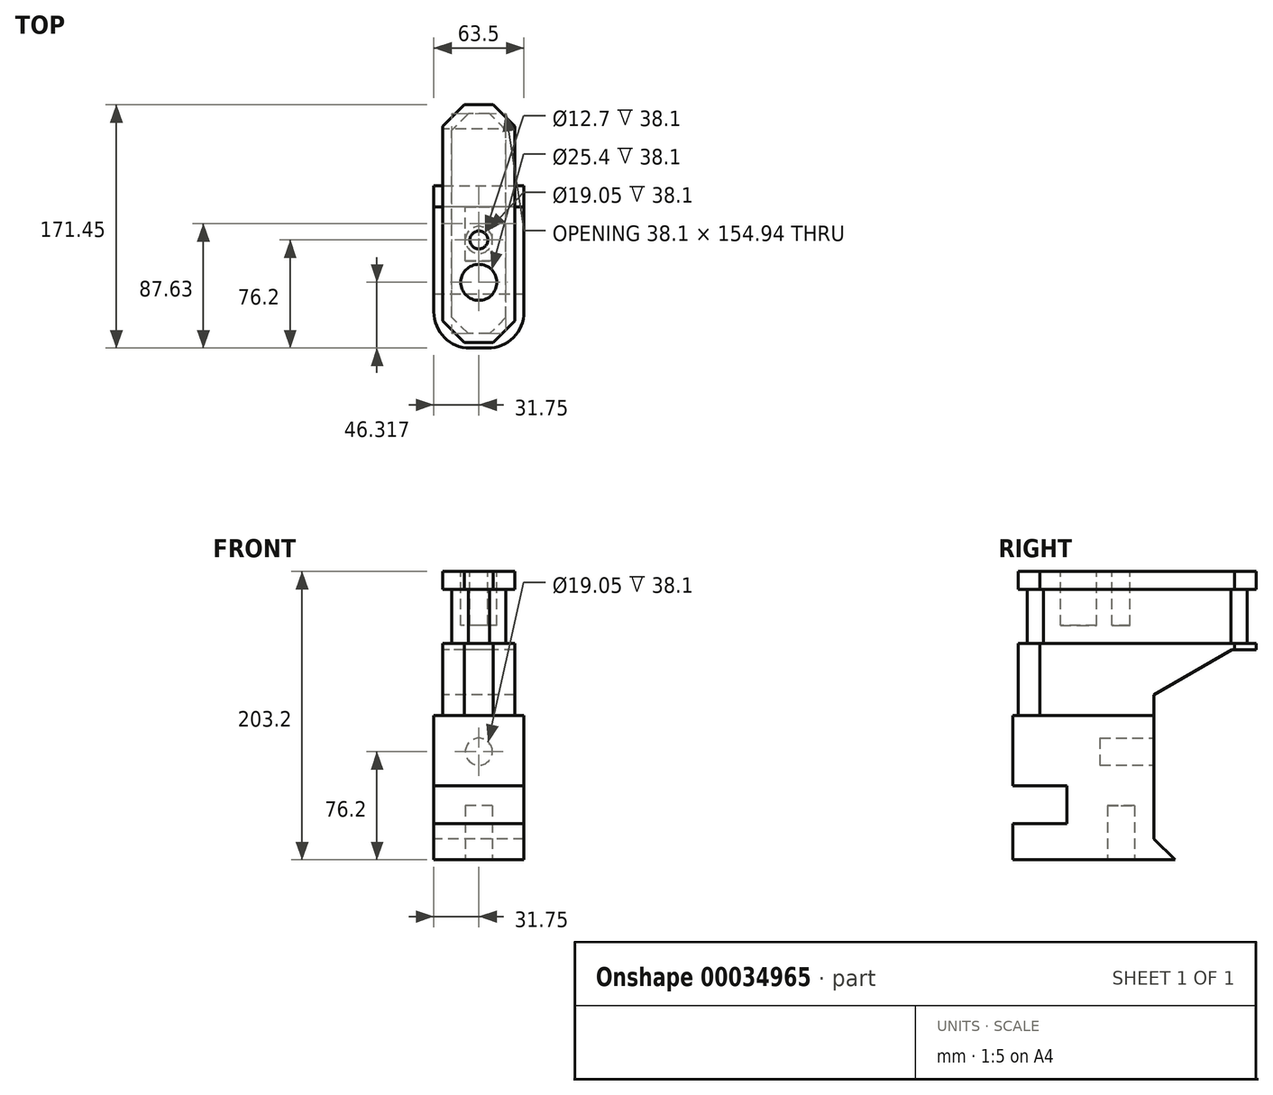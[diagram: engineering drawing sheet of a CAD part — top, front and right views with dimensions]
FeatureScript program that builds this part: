
annotation { "Feature Type Name" : "Feature", "Feature Type Description" : "" }
export const myFeature = defineFeature(function(context is Context, id is Id, definition is map)
    precondition{}
    {
        {
            var Q0;
            Q0=qCreatedBy(makeId("Top.planeOp"),FACE);
            var sketch = newSketch(context, id + "F0", { "sketchPlane" : qUnion([Q0])});
            skCircle(sketch, "E0", {"center": v(0, 0) * mm, "radius": 9.53 * mm});
            skSolve(sketch);
        }
        {
            var Q0;
            Q0=makeQuery(id+"F0.imprint","IMPRINT",FACE,{"disambiguationData":[TD([[makeQuery(id+"F0.imprint","IMPRINT",EDGE,{"derivedFrom":sQuery(id+"F0.wireOp",EDGE,"E0")}),1.0]])]});
            extrude(context, id + "F1", {"entities" : qUnion([Q0]), "depth" : 38.1 * mm});
        }
        {
            var Q0;
            Q0=makeQuery(id+"F1.opExtrude","CAP_FACE",FACE,{"disambiguationData":[OSD([sQuery(id+"F0.wireOp",EDGE,"E0")])],"isStart":false});
            var sketch = newSketch(context, id + "F2", { "sketchPlane" : qUnion([Q0])});
            skLineSegment(sketch, "E1.bottom", {"start": v(-31.75, -76.2) * mm, "end": v(31.75, -76.2) * mm});
            skLineSegment(sketch, "E1.top", {"start": v(-31.75, 38.1) * mm, "end": v(31.75, 38.1) * mm});
            skLineSegment(sketch, "E1.left", {"start": v(-31.75, -76.2) * mm, "end": v(-31.75, 38.1) * mm});
            skLineSegment(sketch, "E1.right", {"start": v(31.75, -76.2) * mm, "end": v(31.75, 38.1) * mm});
            skSolve(sketch);
        }
        {
            var Q0;
            Q0=makeQuery(id+"F2.imprint","IMPRINT",FACE,{"disambiguationData":[TD([[makeQuery(id+"F2.imprint","IMPRINT",EDGE,{"derivedFrom":sQuery(id+"F2.wireOp",EDGE,"E1.bottom")}),1.0]])]});
            var Q1;
            Q1=makeQuery(id+"F2.imprint","IMPRINT",FACE,{"disambiguationData":[TD([[makeQuery(id+"F2.imprint","IMPRINT",EDGE,{"derivedFrom":makeQuery(id+"F1.opExtrude","CAP_EDGE",EDGE,{"disambiguationData":[OSD([sQuery(id+"F0.wireOp",EDGE,"E0")])],"isStart":false})}),1.0]])]});
            extrude(context, id + "F3", {"entities" : qUnion([Q0, Q1]), "operationType" : NewBodyOperationType.ADD, "depth" : 101.6 * mm});
        }
        {
            var Q0;
            Q0=makeQuery(id+"F3.opExtrude","SWEPT_EDGE",EDGE,{"disambiguationData":[OSD([sQuery(id+"F2.wireOp",EDGE,"E1.bottom"),sQuery(id+"F2.wireOp",EDGE,"E1.right")])]});
            var Q1;
            Q1=makeQuery(id+"F3.opExtrude","SWEPT_EDGE",EDGE,{"disambiguationData":[OSD([sQuery(id+"F2.wireOp",EDGE,"E1.bottom"),sQuery(id+"F2.wireOp",EDGE,"E1.left")])]});
            fillet(context, id + "F4", {"entities" : qUnion([Q0, Q1]), "radius" : 25.4 * mm, "tangentPropagation" : true, "allowEdgeOverflow" : false});
        }
        {
            var Q0;
            Q0=makeQuery(id+"F3.opExtrude","CAP_FACE",FACE,{"disambiguationData":[OSD([sQuery(id+"F2.wireOp",EDGE,"E1.bottom"),sQuery(id+"F2.wireOp",EDGE,"E1.top"),sQuery(id+"F2.wireOp",EDGE,"E1.left"),sQuery(id+"F2.wireOp",EDGE,"E1.right")])],"isStart":false});
            var sketch = newSketch(context, id + "F5", { "sketchPlane" : qUnion([Q0])});
            skLineSegment(sketch, "E2.bottom", {"start": v(25.4, -57.15) * mm, "end": v(-25.4, -57.15) * mm});
            skLineSegment(sketch, "E2.top", {"start": v(10.16, 95.25) * mm, "end": v(-10.16, 95.25) * mm});
            skLineSegment(sketch, "E2.left", {"start": v(25.4, -57.15) * mm, "end": v(25.4, 80) * mm});
            skLineSegment(sketch, "E2.right", {"start": v(-25.4, -57.15) * mm, "end": v(-25.4, 80) * mm});
            skLineSegment(sketch, "E3", {"start": v(25.4, -57.15) * mm, "end": v(10.16, -72.4) * mm});
            skLineSegment(sketch, "E4", {"start": v(10.16, -72.4) * mm, "end": v(-10.16, -72.4) * mm});
            skLineSegment(sketch, "E5", {"start": v(-10.16, -72.4) * mm, "end": v(-25.4, -57.15) * mm});
            skLineSegment(sketch, "E6", {"start": v(25.4, 80) * mm, "end": v(10.16, 95.25) * mm});
            skLineSegment(sketch, "E7", {"start": v(-10.16, 95.25) * mm, "end": v(-25.4, 80) * mm});
            skPoint(sketch, "E8.orphan", {"position": v(-25.4, 95.25) * mm});
            skSolve(sketch);
        }
        {
            var Q0;
            Q0=qSketchRegion(id+"F5",true);
            extrude(context, id + "F6", {"entities" : qUnion([Q0]), "operationType" : NewBodyOperationType.ADD, "depth" : 101.6 * mm});
        }
        {
            var Q0;
            Q0=qCreatedBy(makeId("Top.planeOp"),FACE);
            cPlane(context, id + "F7", {"entities" : qUnion([Q0]), "cplaneType" : CPlaneType.OFFSET, "offset" : 190.5 * mm, "width" : 152.4 * mm, "height" : 152.4 * mm});
        }
        {
            var Q0;
            Q0=qCreatedBy(id+"F7.planeOp",FACE);
            var sketch = newSketch(context, id + "F8", { "sketchPlane" : qUnion([Q0])});
            skLineSegment(sketch, "E9.0", {"start": v(-7.53, -66.04) * mm, "end": v(-19.05, -54.52) * mm});
            skLineSegment(sketch, "E9.1", {"start": v(7.53, -66.04) * mm, "end": v(-7.53, -66.04) * mm});
            skLineSegment(sketch, "E9.2", {"start": v(19.05, -54.52) * mm, "end": v(7.53, -66.04) * mm});
            skLineSegment(sketch, "E9.3", {"start": v(19.05, -54.52) * mm, "end": v(19.05, 77.38) * mm});
            skLineSegment(sketch, "E9.4", {"start": v(19.05, 77.38) * mm, "end": v(7.53, 88.9) * mm});
            skLineSegment(sketch, "E9.5", {"start": v(-19.05, -54.52) * mm, "end": v(-19.05, 77.38) * mm});
            skLineSegment(sketch, "E9.6", {"start": v(7.53, 88.9) * mm, "end": v(-7.53, 88.9) * mm});
            skLineSegment(sketch, "E9.7", {"start": v(-7.53, 88.9) * mm, "end": v(-19.05, 77.38) * mm});
            skLineSegment(sketch, "E10.0", {"start": v(-10.16, -72.4) * mm, "end": v(10.16, -72.4) * mm});
            skLineSegment(sketch, "E10.1", {"start": v(-25.4, -57.15) * mm, "end": v(-10.16, -72.4) * mm});
            skLineSegment(sketch, "E10.2", {"start": v(-25.4, 80) * mm, "end": v(-25.4, -57.15) * mm});
            skLineSegment(sketch, "E10.3", {"start": v(-10.16, 95.25) * mm, "end": v(-25.4, 80) * mm});
            skLineSegment(sketch, "E10.4", {"start": v(10.16, 95.25) * mm, "end": v(-10.16, 95.25) * mm});
            skLineSegment(sketch, "E10.5", {"start": v(10.16, -72.4) * mm, "end": v(25.4, -57.15) * mm});
            skLineSegment(sketch, "E10.6", {"start": v(25.4, 80.01) * mm, "end": v(10.16, 95.25) * mm});
            skLineSegment(sketch, "E10.7", {"start": v(25.4, -57.15) * mm, "end": v(25.4, 80.01) * mm});
            skSolve(sketch);
        }
        {
            var Q0;
            Q0=makeQuery(id+"F8.imprint","IMPRINT",FACE,{"disambiguationData":[TD([[makeQuery(id+"F8.imprint","IMPRINT",EDGE,{"derivedFrom":sQuery(id+"F8.wireOp",EDGE,"E9.0")}),1.0]])]});
            extrude(context, id + "F9", {"entities" : qUnion([Q0]), "operationType" : NewBodyOperationType.REMOVE, "depth" : 38.1 * mm});
        }
        {
            var Q0;
            Q0=qCreatedBy(makeId("Right.planeOp"),FACE);
            var sketch = newSketch(context, id + "F10", { "sketchPlane" : qUnion([Q0])});
            skLineSegment(sketch, "E11.0", {"start": v(38.1, 139.7) * mm, "end": v(38.1, 38.1) * mm});
            skLineSegment(sketch, "E11.1", {"start": v(-50.8, 38.1) * mm, "end": v(38.1, 38.1) * mm});
            skLineSegment(sketch, "E11.2", {"start": v(-50.8, 139.7) * mm, "end": v(38.1, 139.7) * mm});
            skLineSegment(sketch, "E12", {"start": v(38.1, 38.1) * mm, "end": v(23.22, 52.98) * mm});
            skLineSegment(sketch, "E13", {"start": v(23.22, 52.98) * mm, "end": v(23.22, 154.58) * mm});
            skLineSegment(sketch, "E14", {"start": v(23.22, 154.58) * mm, "end": v(78.2, 186.33) * mm});
            skLineSegment(sketch, "E15", {"start": v(38.1, 38.1) * mm, "end": v(127, 38.1) * mm});
            skLineSegment(sketch, "E16", {"start": v(78.2, 186.33) * mm, "end": v(116.3, 186.33) * mm});
            skLineSegment(sketch, "E17", {"start": v(116.3, 186.33) * mm, "end": v(419.95, 159.77) * mm});
            skLineSegment(sketch, "E18", {"start": v(419.95, 159.77) * mm, "end": v(523.54, 111.46) * mm});
            skLineSegment(sketch, "E19", {"start": v(127, 38.1) * mm, "end": v(165.5, 60.32) * mm});
            skLineSegment(sketch, "E20", {"start": v(365.08, 0.26) * mm, "end": v(421.84, -9.74) * mm});
            skLineSegment(sketch, "E21", {"start": v(421.84, -9.74) * mm, "end": v(523.54, 111.46) * mm});
            skLineSegment(sketch, "E22", {"start": v(365.08, 0.26) * mm, "end": v(340.6, 29.45) * mm});
            skLineSegment(sketch, "E23", {"start": v(165.5, 60.33) * mm, "end": v(340.6, 29.45) * mm});
            skSolve(sketch);
        }
        {
            var Q0;
            Q0=qSketchRegion(id+"F10",true);
            extrude(context, id + "F11", {"entities" : qUnion([Q0]), "operationType" : NewBodyOperationType.REMOVE, "endBound" : BoundingType.SYMMETRIC, "depth" : 88.9 * mm});
        }
        {
            var Q0;
            Q0=makeQuery(id+"F3.opExtrude","SWEPT_FACE",FACE,{"disambiguationData":[OSD([sQuery(id+"F2.wireOp",EDGE,"E1.right")])]});
            var sketch = newSketch(context, id + "F12", { "sketchPlane" : qUnion([Q0])});
            skLineSegment(sketch, "E24.bottom", {"start": v(-38.1, 63.5) * mm, "end": v(-88.9, 63.5) * mm});
            skLineSegment(sketch, "E24.top", {"start": v(-38.1, 90.17) * mm, "end": v(-88.9, 90.17) * mm});
            skLineSegment(sketch, "E24.left", {"start": v(-38.1, 63.5) * mm, "end": v(-38.1, 90.17) * mm});
            skLineSegment(sketch, "E24.right", {"start": v(-88.9, 63.5) * mm, "end": v(-88.9, 90.17) * mm});
            skSolve(sketch);
        }
        {
            var Q0;
            {var subQ6=sQuery(id+"F12.wireOp",EDGE,"E24.right");Q0=makeQuery(id+"F12.imprint","IMPRINT",FACE,{"disambiguationData":[TD([[makeQuery(id+"F12.imprint","IMPRINT",EDGE,{"derivedFrom":subQ6}),-1.0]])]});}
            var Q1;
            {var subQ6=sQuery(id+"F12.wireOp",EDGE,"E24.left");Q1=makeQuery(id+"F12.imprint","IMPRINT",FACE,{"disambiguationData":[TD([[makeQuery(id+"F12.imprint","IMPRINT",EDGE,{"derivedFrom":subQ6}),1.0]])]});}
            extrude(context, id + "F13", {"entities" : qUnion([Q0, Q1]), "operationType" : NewBodyOperationType.REMOVE, "oppositeDirection" : true, "depth" : 76.2 * mm});
        }
        {
            var Q0;
            Q0=makeQuery(id+"F11.boolean.opBoolean","COPY",FACE,{"derivedFrom":makeQuery(id+"F11.opExtrude","SWEPT_FACE",FACE,{"disambiguationData":[OSD([sQuery(id+"F10.wireOp",EDGE,"E13")])]})});
            var sketch = newSketch(context, id + "F14", { "sketchPlane" : qUnion([Q0])});
            skCircle(sketch, "E25", {"center": v(0, 114.3) * mm, "radius": 9.53 * mm});
            skSolve(sketch);
        }
        {
            var Q0;
            Q0=makeQuery(id+"F14.imprint","IMPRINT",FACE,{"disambiguationData":[TD([[makeQuery(id+"F14.imprint","IMPRINT",EDGE,{"derivedFrom":sQuery(id+"F14.wireOp",EDGE,"E25")}),1.0]])]});
            extrude(context, id + "F15", {"entities" : qUnion([Q0]), "operationType" : NewBodyOperationType.REMOVE, "oppositeDirection" : true, "depth" : 38.1 * mm});
        }
        {
            var Q0;
            Q0=makeQuery(id+"F6.opExtrude","CAP_FACE",FACE,{"disambiguationData":[OSD([sQuery(id+"F5.wireOp",EDGE,"E2.top"),sQuery(id+"F5.wireOp",EDGE,"E2.left"),sQuery(id+"F5.wireOp",EDGE,"E2.right"),sQuery(id+"F5.wireOp",EDGE,"E3"),sQuery(id+"F5.wireOp",EDGE,"E4"),sQuery(id+"F5.wireOp",EDGE,"E5"),sQuery(id+"F5.wireOp",EDGE,"E6"),sQuery(id+"F5.wireOp",EDGE,"E7")])],"isStart":false});
            var sketch = newSketch(context, id + "F16", { "sketchPlane" : qUnion([Q0])});
            skCircle(sketch, "E26", {"center": v(0, -29.88) * mm, "radius": 12.7 * mm});
            skCircle(sketch, "E27", {"center": v(0, 0) * mm, "radius": 6.35 * mm});
            skSolve(sketch);
        }
        {
            var Q0;
            Q0=makeQuery(id+"F16.imprint","IMPRINT",FACE,{"disambiguationData":[TD([[makeQuery(id+"F16.imprint","IMPRINT",EDGE,{"derivedFrom":sQuery(id+"F16.wireOp",EDGE,"E26")}),1.0]])]});
            var Q1;
            Q1=makeQuery(id+"F16.imprint","IMPRINT",FACE,{"disambiguationData":[TD([[makeQuery(id+"F16.imprint","IMPRINT",EDGE,{"derivedFrom":sQuery(id+"F16.wireOp",EDGE,"E27")}),1.0]])]});
            extrude(context, id + "F17", {"entities" : qUnion([Q0, Q1]), "operationType" : NewBodyOperationType.REMOVE, "oppositeDirection" : true, "depth" : 38.1 * mm});
        }
        {
            var Q0;
            Q0=makeQuery(id+"F1.opExtrude","CAP_FACE",FACE,{"disambiguationData":[OSD([sQuery(id+"F0.wireOp",EDGE,"E0")])],"isStart":true});
            extrude(context, id + "F18", {"entities" : qUnion([Q0]), "operationType" : NewBodyOperationType.REMOVE, "oppositeDirection" : true, "depth" : 76.2 * mm});
        }
    });
